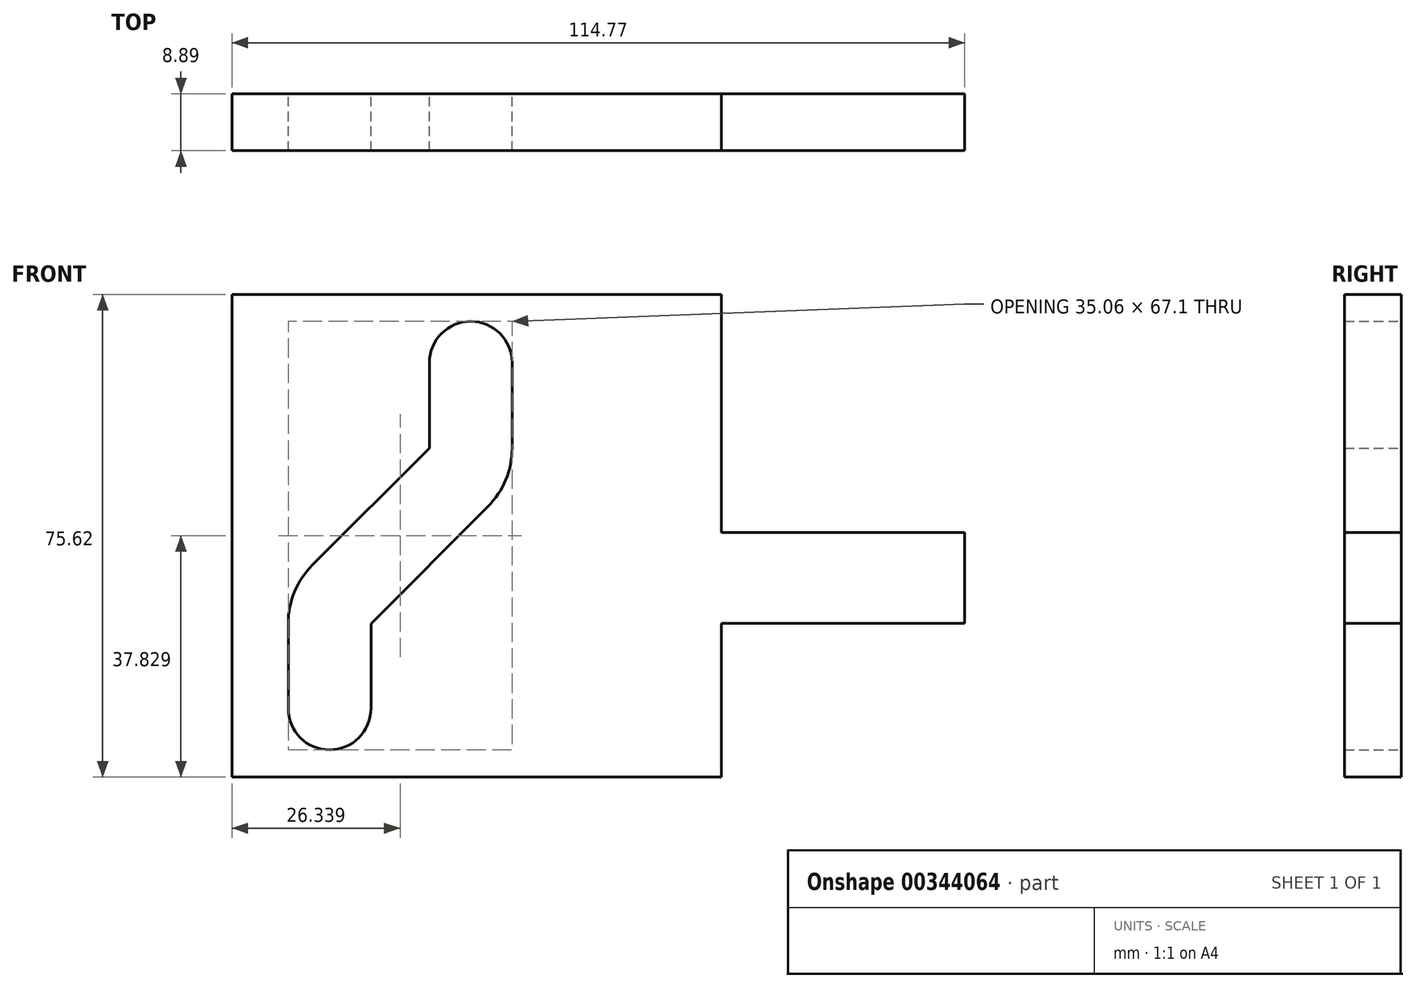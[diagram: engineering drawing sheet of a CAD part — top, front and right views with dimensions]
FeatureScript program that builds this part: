
annotation { "Feature Type Name" : "Feature", "Feature Type Description" : "" }
export const myFeature = defineFeature(function(context is Context, id is Id, definition is map)
    precondition{}
    {
        {
            var Q0;
            Q0=qCreatedBy(makeId("Front.planeOp"),FACE);
            var sketch = newSketch(context, id + "F0", { "sketchPlane" : qUnion([Q0])});
            skLineSegment(sketch, "E0", {"start": v(0, 0) * mm, "end": v(0, 50.8) * mm});
            skLineSegment(sketch, "E1", {"start": v(-5.61, 5.61) * mm, "end": v(3.55, 14.77) * mm});
            skLineSegment(sketch, "E2.MirrorCS", {"start": v(-5.61, 5.61) * mm, "end": v(-14.77, -3.55) * mm});
            skLineSegment(sketch, "E3.MirrorCS", {"start": v(3.55, -3.54) * mm, "end": v(-5.6, -12.7) * mm});
            skLineSegment(sketch, "E4", {"start": v(-5.61, 5.61) * mm, "end": v(-14.77, -3.54) * mm});
            skLineSegment(sketch, "E5", {"start": v(3.55, -3.54) * mm, "end": v(12.7, 5.61) * mm});
            skPoint(sketch, "E6.visualSharp", {"position": v(16.5, 9.4) * mm});
            skArc(sketch, "E6.filletArc", {"start": v(12.7, 5.61) * mm, "mid": v(15.51, 9.81) * mm, "end": v(16.5, 14.77) * mm});
            skPoint(sketch, "E7.visualSharp", {"position": v(-18.56, -7.34) * mm});
            skArc(sketch, "E7.filletArc", {"start": v(-14.77, -3.54) * mm, "mid": v(-17.58, -7.75) * mm, "end": v(-18.56, -12.7) * mm});
            skPoint(sketch, "E8.first.point", {"position": v(-5.6, -26.77) * mm});
            skPoint(sketch, "E8.second.point", {"position": v(-18.56, -26) * mm});
            skLineSegment(sketch, "E9", {"start": v(-5.6, -12.7) * mm, "end": v(-5.6, -26) * mm});
            skArc(sketch, "E10", {"start": v(-18.56, -26) * mm, "mid": v(-12.09, -32.48) * mm, "end": v(-5.6, -26) * mm});
            skLineSegment(sketch, "E11", {"start": v(-18.56, -12.7) * mm, "end": v(-18.56, -26) * mm});
            skLineSegment(sketch, "E12", {"start": v(16.5, 14.77) * mm, "end": v(16.5, 28.14) * mm});
            skLineSegment(sketch, "E13", {"start": v(3.55, 14.77) * mm, "end": v(3.55, 28.14) * mm});
            skArc(sketch, "E14", {"start": v(16.5, 28.14) * mm, "mid": v(10.02, 34.62) * mm, "end": v(3.55, 28.14) * mm});
            skLineSegment(sketch, "E15.right", {"start": v(-27.37, 1.92) * mm, "end": v(-27.37, 38.86) * mm});
            skPoint(sketch, "E16.endSnap0", {"position": v(-12.09, -32.48) * mm});
            skLineSegment(sketch, "E17", {"start": v(-27.37, 1.92) * mm, "end": v(-27.37, -36.76) * mm});
            skLineSegment(sketch, "E18", {"start": v(87.4, -5.54) * mm, "end": v(87.4, 1.57) * mm});
            skLineSegment(sketch, "E19.MirrorCS", {"start": v(87.4, -5.54) * mm, "end": v(87.4, -12.65) * mm});
            skLineSegment(sketch, "E20", {"start": v(87.4, 1.57) * mm, "end": v(49.28, 1.57) * mm});
            skLineSegment(sketch, "E21.MirrorCS", {"start": v(87.4, -12.65) * mm, "end": v(49.28, -12.65) * mm});
            skLineSegment(sketch, "E22", {"start": v(49.28, 1.57) * mm, "end": v(49.28, 38.86) * mm});
            skLineSegment(sketch, "E23", {"start": v(49.28, -12.65) * mm, "end": v(49.28, -36.76) * mm});
            skLineSegment(sketch, "E24", {"start": v(-27.37, 38.86) * mm, "end": v(49.28, 38.86) * mm});
            skLineSegment(sketch, "E25", {"start": v(-27.37, -36.76) * mm, "end": v(49.28, -36.76) * mm});
            skSolve(sketch);
        }
        {
            var Q0;
            Q0 = qSketchRegion(id + "F0", true);
            extrude(context, id + "F1", {"entities" : qUnion([Q0]), "depth" : 8.9 * mm});
        }
    });
